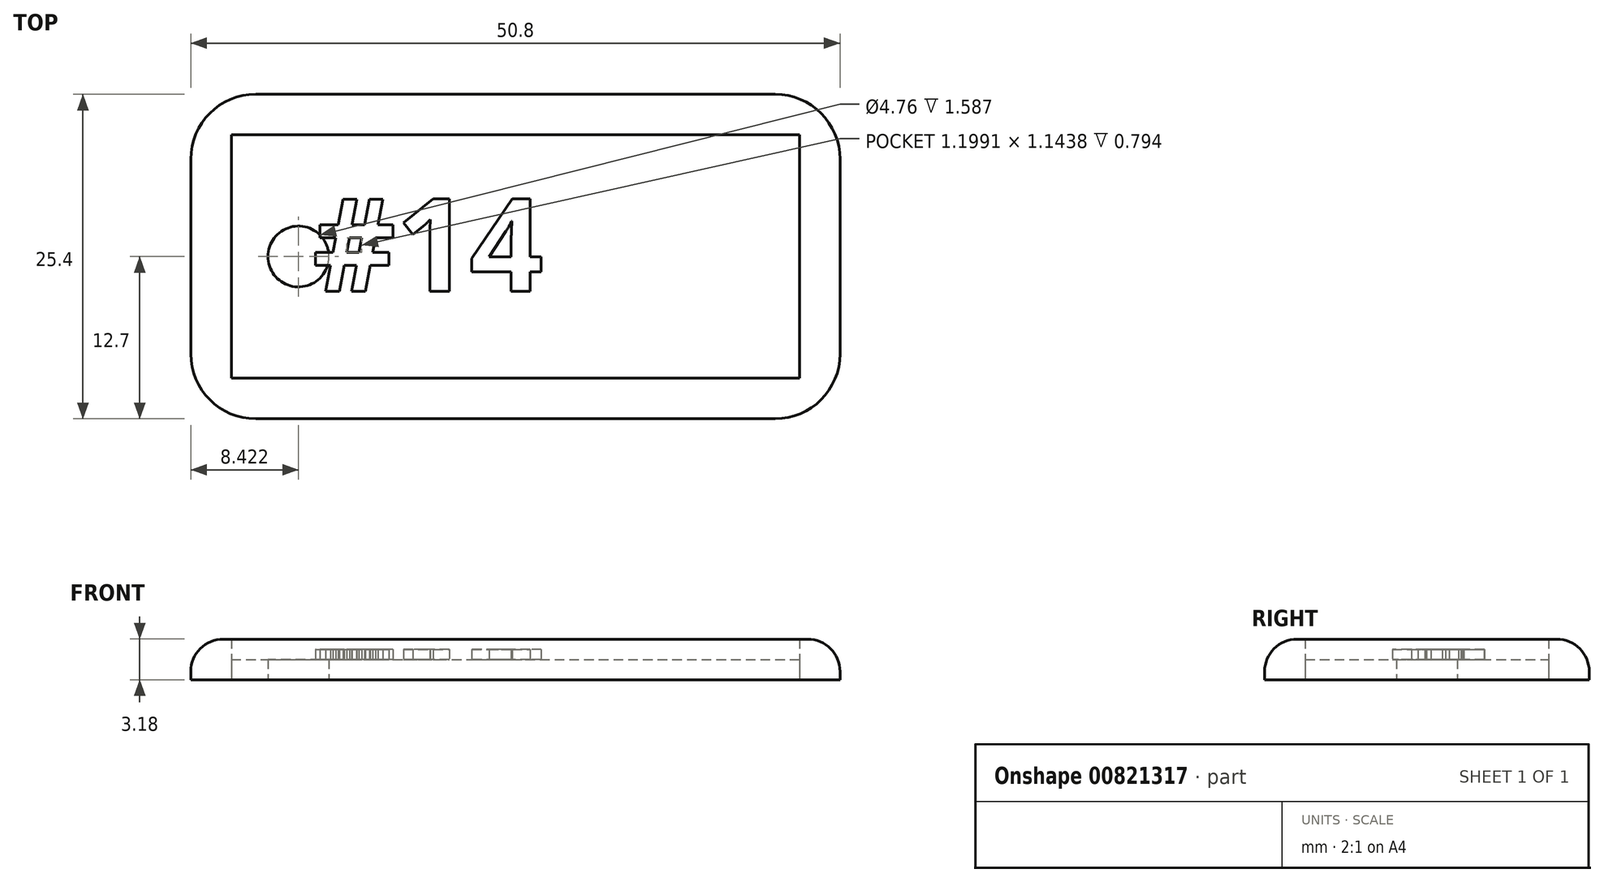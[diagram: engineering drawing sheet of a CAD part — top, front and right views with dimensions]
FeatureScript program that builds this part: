
annotation { "Feature Type Name" : "Feature", "Feature Type Description" : "" }
export const myFeature = defineFeature(function(context is Context, id is Id, definition is map)
    precondition{}
    {
        {
            var Q0;
            Q0=qCreatedBy(makeId("Top.planeOp"),FACE);
            var sketch = newSketch(context, id + "F0", { "sketchPlane" : qUnion([Q0])});
            skLineSegment(sketch, "E0.bottom", {"start": v(0, 0) * mm, "end": v(50.8, 0) * mm});
            skLineSegment(sketch, "E0.top", {"start": v(0, 25.4) * mm, "end": v(50.8, 25.4) * mm});
            skLineSegment(sketch, "E0.left", {"start": v(0, 0) * mm, "end": v(0, 25.4) * mm});
            skLineSegment(sketch, "E0.right", {"start": v(50.8, 0) * mm, "end": v(50.8, 25.4) * mm});
            skCircle(sketch, "E1", {"center": v(8.42, 12.7) * mm, "radius": 2.38 * mm});
            skPoint(sketch, "E1.centerSnap0", {"position": v(0, 12.7) * mm});
            skLineSegment(sketch, "E2.0", {"start": v(3.17, 22.23) * mm, "end": v(47.62, 22.23) * mm});
            skLineSegment(sketch, "E2.1", {"start": v(3.18, 3.18) * mm, "end": v(3.17, 22.23) * mm});
            skLineSegment(sketch, "E2.2", {"start": v(3.18, 3.18) * mm, "end": v(47.62, 3.18) * mm});
            skLineSegment(sketch, "E2.3", {"start": v(47.62, 3.18) * mm, "end": v(47.62, 22.23) * mm});
            skSolve(sketch);
        }
        {
            var Q0;
            Q0=makeQuery(id+"F0.imprint","IMPRINT",FACE,{"disambiguationData":[TD([[makeQuery(id+"F0.imprint","IMPRINT",EDGE,{"derivedFrom":sQuery(id+"F0.wireOp",EDGE,"E0.bottom")}),1.0]])]});
            var Q1;
            Q1=sQuery(id+"F0.wireOp",EDGE,"E0.bottom");
            var Q2;
            Q2=sQuery(id+"F0.wireOp",EDGE,"E0.left");
            extrude(context, id + "F1", {"entities" : qUnion([Q0]), "surfaceEntities" : qUnion([Q1, Q2]), "depth" : 3.17 * mm, "offsetDistance" : 25.4 * mm});
        }
        {
            var Q0;
            Q0=makeQuery(id+"F0.imprint","IMPRINT",FACE,{"disambiguationData":[TD([[makeQuery(id+"F0.imprint","IMPRINT",EDGE,{"derivedFrom":sQuery(id+"F0.wireOp",EDGE,"E1")}),-1.0]])]});
            extrude(context, id + "F2", {"entities" : qUnion([Q0]), "depth" : 1.59 * mm, "offsetDistance" : 25.4 * mm});
        }
        {
            var Q0;
            Q0=makeQuery(id+"F1.opExtrude","SWEPT_EDGE",EDGE,{"disambiguationData":[OSD([sQuery(id+"F0.wireOp",EDGE,"E0.bottom"),sQuery(id+"F0.wireOp",EDGE,"E0.left")])]});
            var Q1;
            Q1=makeQuery(id+"F1.opExtrude","SWEPT_EDGE",EDGE,{"disambiguationData":[OSD([sQuery(id+"F0.wireOp",EDGE,"E0.bottom"),sQuery(id+"F0.wireOp",EDGE,"E0.right")])]});
            var Q2;
            Q2=makeQuery(id+"F1.opExtrude","SWEPT_EDGE",EDGE,{"disambiguationData":[OSD([sQuery(id+"F0.wireOp",EDGE,"E0.top"),sQuery(id+"F0.wireOp",EDGE,"E0.right")])]});
            var Q3;
            Q3=makeQuery(id+"F1.opExtrude","SWEPT_EDGE",EDGE,{"disambiguationData":[OSD([sQuery(id+"F0.wireOp",EDGE,"E0.top"),sQuery(id+"F0.wireOp",EDGE,"E0.left")])]});
            fillet(context, id + "F3", {"entities" : qUnion([Q0, Q1, Q2, Q3]), "radius" : 5.08 * mm, "tangentPropagation" : true, "allowEdgeOverflow" : false});
        }
        {
            var Q0;
            Q0=makeQuery(id+"F1.opExtrude","CAP_EDGE",EDGE,{"disambiguationData":[OSD([sQuery(id+"F0.wireOp",EDGE,"E0.bottom")])],"isStart":false});
            var Q1;
            Q1=makeQuery(id+"F1.opExtrude","CAP_EDGE",EDGE,{"disambiguationData":[OSD([sQuery(id+"F0.wireOp",EDGE,"E0.left")])],"isStart":false});
            var Q2;
            Q2=makeQuery(id+"F1.opExtrude","CAP_EDGE",EDGE,{"disambiguationData":[OSD([sQuery(id+"F0.wireOp",EDGE,"E0.right")])],"isStart":false});
            var Q3;
            Q3=makeQuery(id+"F1.opExtrude","CAP_EDGE",EDGE,{"disambiguationData":[OSD([sQuery(id+"F0.wireOp",EDGE,"E0.top")])],"isStart":false});
            fillet(context, id + "F4", {"entities" : qUnion([Q0, Q1, Q2, Q3]), "radius" : 2.54 * mm, "tangentPropagation" : true, "allowEdgeOverflow" : false});
        }
        {
            var Q0;
            Q0=makeQuery(id+"F2.opExtrude","CAP_FACE",FACE,{"disambiguationData":[OSD([sQuery(id+"F0.wireOp",EDGE,"E1"),sQuery(id+"F0.wireOp",EDGE,"E2.0"),sQuery(id+"F0.wireOp",EDGE,"E2.1"),sQuery(id+"F0.wireOp",EDGE,"E2.2"),sQuery(id+"F0.wireOp",EDGE,"E2.3")])],"isStart":false});
            var sketch = newSketch(context, id + "F5", { "sketchPlane" : qUnion([Q0])});
            skText(sketch, "E3", { "text": "#14", "fontName": "OpenSans-Bold.ttf"});
            const initialGuessF5  = {"E3": [0.00953, 0.00999, 1, 0, 0.00727]};
            skSetInitialGuess(sketch, initialGuessF5);
            skSolve(sketch);
        }
        {
            var Q0;
            Q0 = qSketchRegion(id + "F5", true);
            extrude(context, id + "F6", {"entities" : qUnion([Q0]), "operationType" : NewBodyOperationType.ADD, "depth" : 0.8 * mm, "offsetDistance" : 25.4 * mm});
        }
    });
